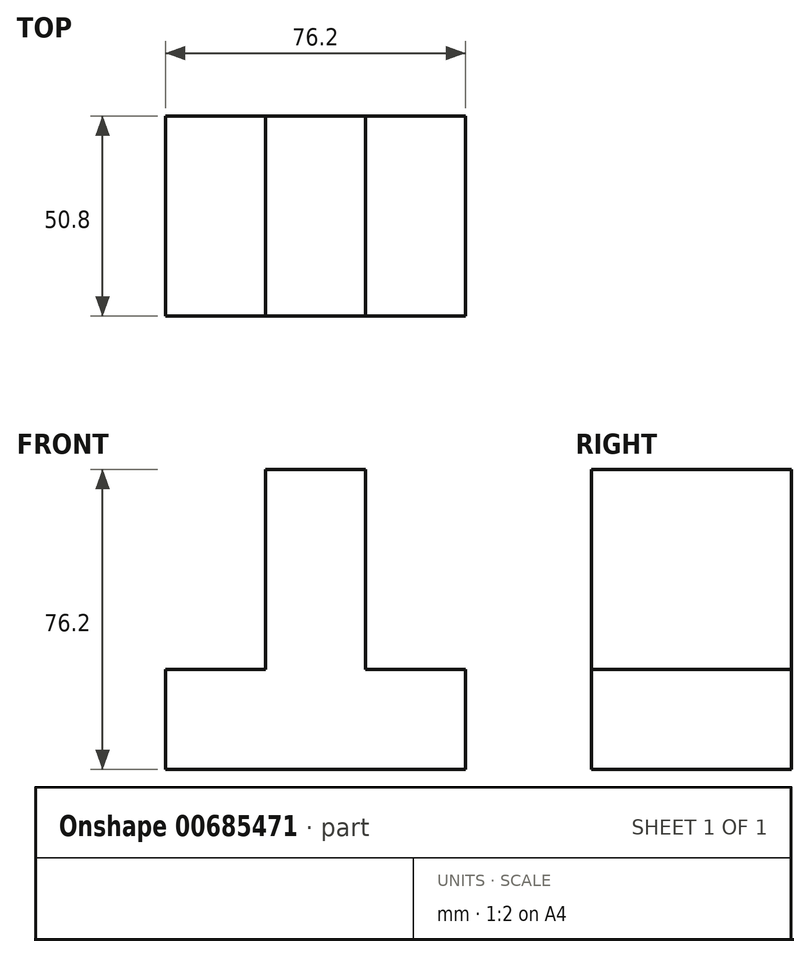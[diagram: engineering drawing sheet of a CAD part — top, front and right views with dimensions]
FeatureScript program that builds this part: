
annotation { "Feature Type Name" : "Feature", "Feature Type Description" : "" }
export const myFeature = defineFeature(function(context is Context, id is Id, definition is map)
    precondition{}
    {
        {
            var Q0;
            Q0=qCreatedBy(makeId("Front.planeOp"),FACE);
            var sketch = newSketch(context, id + "F0", { "sketchPlane" : qUnion([Q0])});
            skLineSegment(sketch, "E0", {"start": v(-26.64, 6.97) * mm, "end": v(-52.04, 6.97) * mm});
            skLineSegment(sketch, "E1", {"start": v(-52.04, 6.97) * mm, "end": v(-52.04, -18.43) * mm});
            skLineSegment(sketch, "E2", {"start": v(-52.04, -18.43) * mm, "end": v(24.16, -18.43) * mm});
            skLineSegment(sketch, "E3", {"start": v(24.16, -18.43) * mm, "end": v(24.16, 6.97) * mm});
            skLineSegment(sketch, "E4", {"start": v(24.16, 6.97) * mm, "end": v(-1.24, 6.97) * mm});
            skLineSegment(sketch, "E5", {"start": v(-1.24, 6.97) * mm, "end": v(-1.24, 57.77) * mm});
            skLineSegment(sketch, "E6", {"start": v(-1.24, 57.77) * mm, "end": v(-26.64, 57.77) * mm});
            skLineSegment(sketch, "E7", {"start": v(-26.64, 57.77) * mm, "end": v(-26.64, 6.97) * mm});
            skSolve(sketch);
        }
        {
            var Q0;
            Q0=makeQuery(id+"F0.imprint","IMPRINT",FACE,{"disambiguationData":[TD([[makeQuery(id+"F0.imprint","IMPRINT",EDGE,{"derivedFrom":sQuery(id+"F0.wireOp",EDGE,"E0")}),1.0]])]});
            extrude(context, id + "F1", {"entities" : qUnion([Q0]), "depth" : 50.8 * mm, "offsetDistance" : 25.4 * mm});
        }
    });
